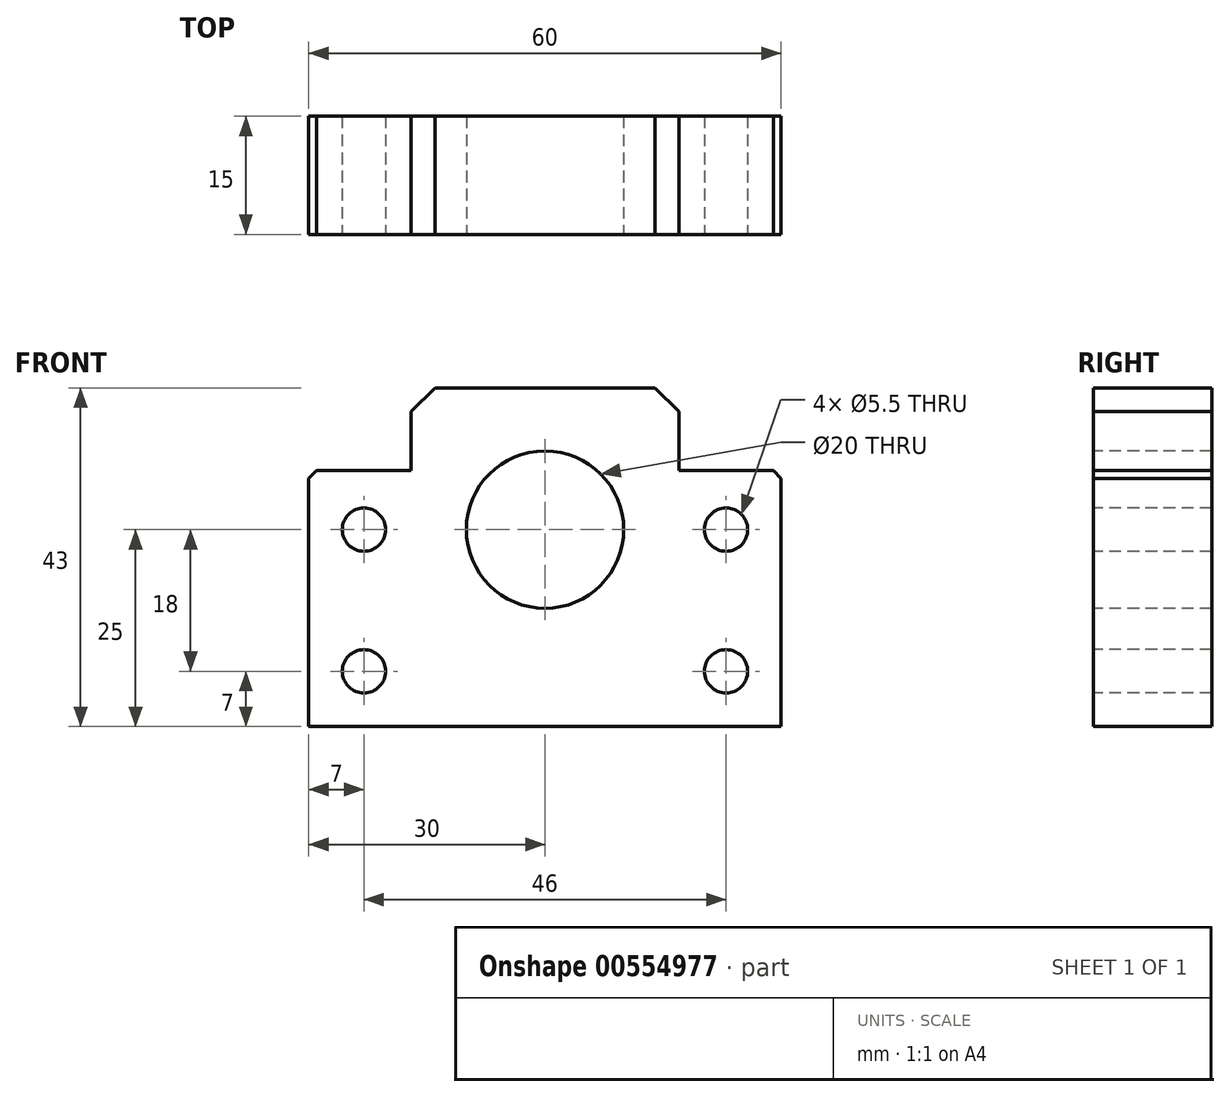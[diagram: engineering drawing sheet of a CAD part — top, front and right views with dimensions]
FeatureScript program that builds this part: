
annotation { "Feature Type Name" : "Feature", "Feature Type Description" : "" }
export const myFeature = defineFeature(function(context is Context, id is Id, definition is map)
    precondition{}
    {
        {
            var Q0;
            Q0=qCreatedBy(makeId("Front.planeOp"),FACE);
            var sketch = newSketch(context, id + "F0", { "sketchPlane" : qUnion([Q0])});
            skLineSegment(sketch, "E0.bottom", {"start": v(17, 21.5) * mm, "end": v(-17, 21.5) * mm});
            skLineSegment(sketch, "E0.top", {"start": v(30, -21.5) * mm, "end": v(-30, -21.5) * mm});
            skLineSegment(sketch, "E0.left", {"start": v(30, 11) * mm, "end": v(30, -21.5) * mm});
            skLineSegment(sketch, "E0.right", {"start": v(-30, 11) * mm, "end": v(-30, -21.5) * mm});
            skPoint(sketch, "E0.middle", {"position": v(0, 0) * mm});
            skLineSegment(sketch, "E1", {"start": v(-17, 21.5) * mm, "end": v(-17, 11) * mm});
            skLineSegment(sketch, "E2", {"start": v(-17, 11) * mm, "end": v(-30, 11) * mm});
            skLineSegment(sketch, "E3", {"start": v(17, 21.5) * mm, "end": v(17, 11) * mm});
            skLineSegment(sketch, "E4", {"start": v(17, 11) * mm, "end": v(30, 11) * mm});
            skPoint(sketch, "E5.orphan", {"position": v(-30, 21.5) * mm});
            skPoint(sketch, "E6.orphan", {"position": v(30, 21.5) * mm});
            skSolve(sketch);
        }
        {
            var Q0;
            Q0 = qSketchRegion(id + "F0", true);
            extrude(context, id + "F1", {"entities" : qUnion([Q0]), "endBound" : BoundingType.SYMMETRIC, "depth" : 15 * mm, "offsetDistance" : 25 * mm});
        }
        {
            var Q0;
            Q0=makeQuery(id+"F1.opExtrude","CAP_FACE",FACE,{"disambiguationData":[OSD([sQuery(id+"F0.wireOp",EDGE,"E0.bottom"),sQuery(id+"F0.wireOp",EDGE,"E0.top"),sQuery(id+"F0.wireOp",EDGE,"E0.left"),sQuery(id+"F0.wireOp",EDGE,"E0.right"),sQuery(id+"F0.wireOp",EDGE,"E1"),sQuery(id+"F0.wireOp",EDGE,"E2"),sQuery(id+"F0.wireOp",EDGE,"E3"),sQuery(id+"F0.wireOp",EDGE,"E4")])],"isStart":false});
            var sketch = newSketch(context, id + "F2", { "sketchPlane" : qUnion([Q0])});
            skCircle(sketch, "E7", {"center": v(0, 3.5) * mm, "radius": 10 * mm});
            skCircle(sketch, "E8", {"center": v(-23, 3.5) * mm, "radius": 2.75 * mm});
            skCircle(sketch, "E9", {"center": v(23, 3.5) * mm, "radius": 2.75 * mm});
            skCircle(sketch, "E10", {"center": v(-23, -14.5) * mm, "radius": 2.75 * mm});
            skCircle(sketch, "E11", {"center": v(23, -14.5) * mm, "radius": 2.75 * mm});
            skSolve(sketch);
        }
        {
            var Q0;
            Q0 = qSketchRegion(id + "F2", true);
            extrude(context, id + "F3", {"entities" : qUnion([Q0]), "operationType" : NewBodyOperationType.REMOVE, "oppositeDirection" : true, "depth" : 15 * mm, "offsetDistance" : 25 * mm});
        }
        {
            var Q0;
            Q0=makeQuery(id+"F1.opExtrude","SWEPT_EDGE",EDGE,{"disambiguationData":[OSD([sQuery(id+"F0.wireOp",EDGE,"E0.bottom"),sQuery(id+"F0.wireOp",EDGE,"E3")])]});
            var Q1;
            Q1=makeQuery(id+"F1.opExtrude","SWEPT_EDGE",EDGE,{"disambiguationData":[OSD([sQuery(id+"F0.wireOp",EDGE,"E0.bottom"),sQuery(id+"F0.wireOp",EDGE,"E1")])]});
            chamfer(context, id + "F4", {"entities" : qUnion([Q0, Q1]), "width" : 3 * mm, "tangentPropagation" : true});
        }
        {
            var Q0;
            Q0=makeQuery(id+"F1.opExtrude","SWEPT_EDGE",EDGE,{"disambiguationData":[OSD([sQuery(id+"F0.wireOp",EDGE,"E0.right"),sQuery(id+"F0.wireOp",EDGE,"E2")])]});
            var Q1;
            Q1=makeQuery(id+"F1.opExtrude","SWEPT_EDGE",EDGE,{"disambiguationData":[OSD([sQuery(id+"F0.wireOp",EDGE,"E0.left"),sQuery(id+"F0.wireOp",EDGE,"E4")])]});
            chamfer(context, id + "F5", {"entities" : qUnion([Q0, Q1]), "width" : 1 * mm, "tangentPropagation" : true});
        }
    });
